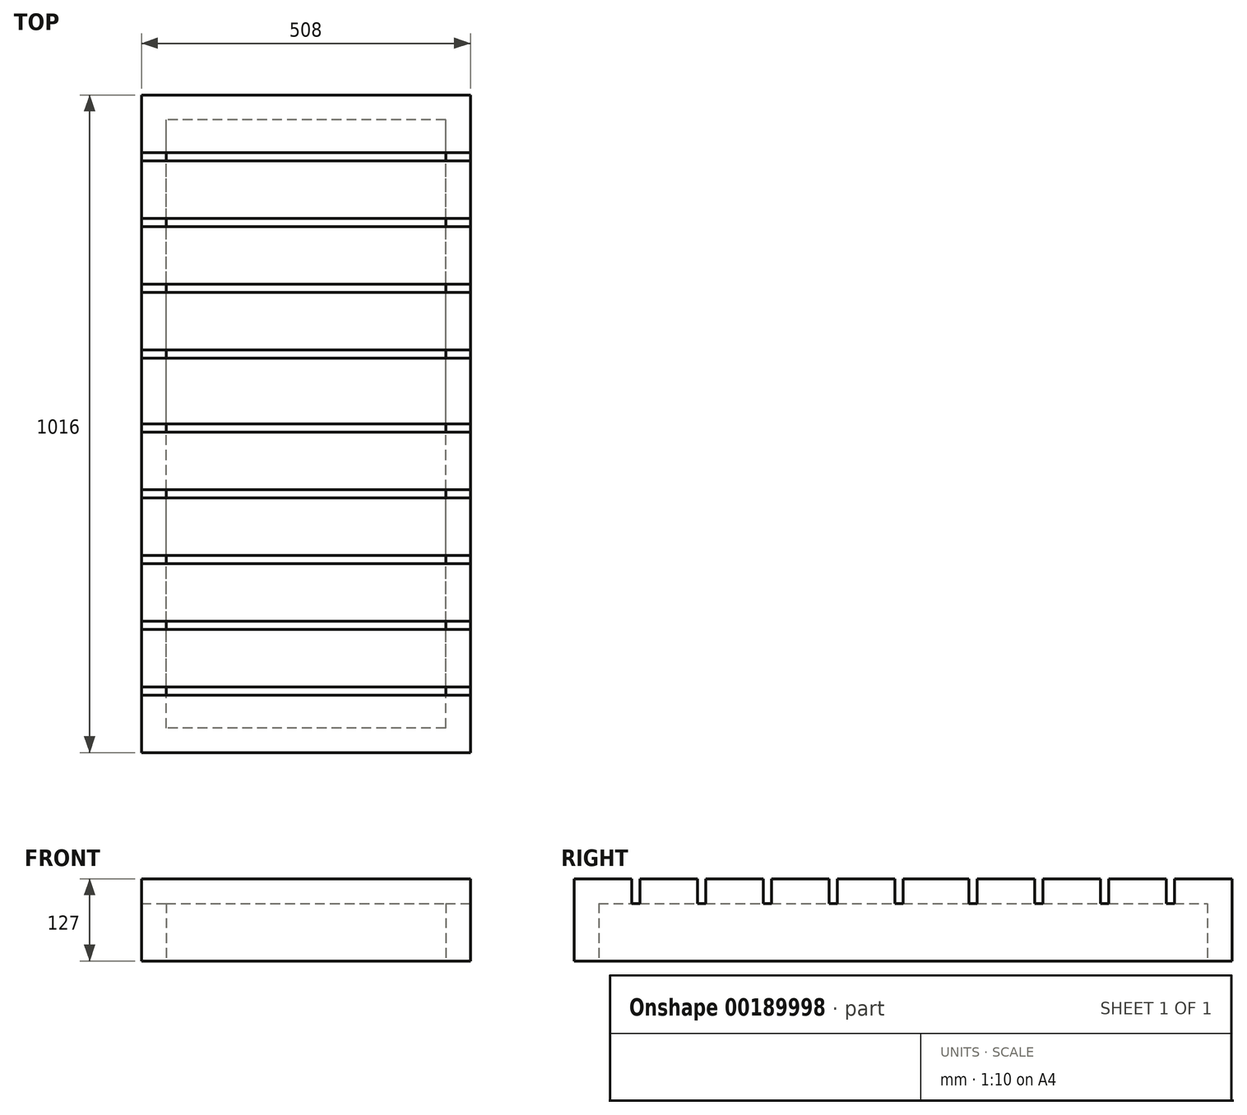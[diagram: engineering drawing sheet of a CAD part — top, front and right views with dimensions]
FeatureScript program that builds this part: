
annotation { "Feature Type Name" : "Feature", "Feature Type Description" : "" }
export const myFeature = defineFeature(function(context is Context, id is Id, definition is map)
    precondition{}
    {
        {
            var Q0;
            Q0=qCreatedBy(makeId("Top.planeOp"),FACE);
            var sketch = newSketch(context, id + "F0", { "sketchPlane" : qUnion([Q0])});
            skLineSegment(sketch, "E0.bottom", {"start": v(254, 508) * mm, "end": v(-254, 508) * mm});
            skLineSegment(sketch, "E0.top", {"start": v(254, -508) * mm, "end": v(-254, -508) * mm});
            skLineSegment(sketch, "E0.left", {"start": v(254, 508) * mm, "end": v(254, -508) * mm});
            skLineSegment(sketch, "E0.right", {"start": v(-254, 508) * mm, "end": v(-254, -508) * mm});
            skPoint(sketch, "E0.middle", {"position": v(0, 0) * mm});
            skSolve(sketch);
        }
        {
            var Q0;
            Q0=makeQuery(id+"F0.imprint","IMPRINT",FACE,{"disambiguationData":[TD([[makeQuery(id+"F0.imprint","IMPRINT",EDGE,{"derivedFrom":sQuery(id+"F0.wireOp",EDGE,"E0.bottom")}),1.0]])]});
            extrude(context, id + "F1", {"entities" : qUnion([Q0]), "depth" : 88.9 * mm});
        }
        {
            var Q0;
            Q0=makeQuery(id+"F1.opExtrude","CAP_FACE",FACE,{"disambiguationData":[OSD([sQuery(id+"F0.wireOp",EDGE,"E0.bottom"),sQuery(id+"F0.wireOp",EDGE,"E0.top"),sQuery(id+"F0.wireOp",EDGE,"E0.left"),sQuery(id+"F0.wireOp",EDGE,"E0.right")])],"isStart":true});
            var sketch = newSketch(context, id + "F2", { "sketchPlane" : qUnion([Q0])});
            skLineSegment(sketch, "E1.bottom", {"start": v(215.9, 469.9) * mm, "end": v(-215.9, 469.9) * mm});
            skLineSegment(sketch, "E1.top", {"start": v(215.9, -469.9) * mm, "end": v(-215.9, -469.9) * mm});
            skLineSegment(sketch, "E1.left", {"start": v(215.9, 469.9) * mm, "end": v(215.9, -469.9) * mm});
            skLineSegment(sketch, "E1.right", {"start": v(-215.9, 469.9) * mm, "end": v(-215.9, -469.9) * mm});
            skSolve(sketch);
        }
        {
            var Q0;
            Q0 = qSketchRegion(id + "F2", true);
            extrude(context, id + "F6", {"entities" : qUnion([Q0]), "operationType" : NewBodyOperationType.REMOVE, "oppositeDirection" : true, "depth" : 88.9 * mm});
        }
        {
            var Q0;
            Q0=makeQuery(id+"F1.opExtrude","CAP_FACE",FACE,{"disambiguationData":[OSD([sQuery(id+"F0.wireOp",EDGE,"E0.bottom"),sQuery(id+"F0.wireOp",EDGE,"E0.top"),sQuery(id+"F0.wireOp",EDGE,"E0.left"),sQuery(id+"F0.wireOp",EDGE,"E0.right")])],"isStart":false});
            var sketch = newSketch(context, id + "F3", { "sketchPlane" : qUnion([Q0])});
            skLineSegment(sketch, "E2.bottom", {"start": v(-254, 508) * mm, "end": v(254, 508) * mm});
            skLineSegment(sketch, "E2.left", {"start": v(-254, 508) * mm, "end": v(-254, -508) * mm});
            skLineSegment(sketch, "E2.right", {"start": v(254, 508) * mm, "end": v(254, -508) * mm});
            skLineSegment(sketch, "E3", {"start": v(-254, -508) * mm, "end": v(254, -508) * mm});
            skSolve(sketch);
        }
        {
            var Q0;
            Q0 = qSketchRegion(id + "F3", true);
            extrude(context, id + "F4", {"entities" : qUnion([Q0]), "operationType" : NewBodyOperationType.ADD, "depth" : 38.1 * mm});
        }
        {
            var Q0;
            Q0=makeQuery(id+"F4.opExtrude","CAP_FACE",FACE,{"disambiguationData":[OSD([sQuery(id+"F3.wireOp",EDGE,"E2.bottom"),sQuery(id+"F3.wireOp",EDGE,"E2.left"),sQuery(id+"F3.wireOp",EDGE,"E2.right"),sQuery(id+"F3.wireOp",EDGE,"E3")])],"isStart":false});
            var sketch = newSketch(context, id + "F5", { "sketchPlane" : qUnion([Q0])});
            skLineSegment(sketch, "E4.bottom", {"start": v(-254, 419.1) * mm, "end": v(254, 419.1) * mm});
            skLineSegment(sketch, "E4.top", {"start": v(-254, 406.4) * mm, "end": v(254, 406.4) * mm});
            skLineSegment(sketch, "E4.left", {"start": v(-254, 419.1) * mm, "end": v(-254, 406.4) * mm});
            skLineSegment(sketch, "E4.right", {"start": v(254, 419.1) * mm, "end": v(254, 406.4) * mm});
            skLineSegment(sketch, "E5.bottom", {"start": v(-254, 317.5) * mm, "end": v(254, 317.5) * mm});
            skLineSegment(sketch, "E5.top", {"start": v(-254, 304.8) * mm, "end": v(254, 304.8) * mm});
            skLineSegment(sketch, "E5.left", {"start": v(-254, 317.5) * mm, "end": v(-254, 304.8) * mm});
            skLineSegment(sketch, "E5.right", {"start": v(254, 317.5) * mm, "end": v(254, 304.8) * mm});
            skLineSegment(sketch, "E6.bottom", {"start": v(-254, 215.9) * mm, "end": v(254, 215.9) * mm});
            skLineSegment(sketch, "E6.top", {"start": v(-254, 203.2) * mm, "end": v(254, 203.2) * mm});
            skLineSegment(sketch, "E6.left", {"start": v(-254, 215.9) * mm, "end": v(-254, 203.2) * mm});
            skLineSegment(sketch, "E6.right", {"start": v(254, 215.9) * mm, "end": v(254, 203.2) * mm});
            skLineSegment(sketch, "E7.bottom", {"start": v(-254, 114.3) * mm, "end": v(254, 114.3) * mm});
            skLineSegment(sketch, "E7.top", {"start": v(-254, 101.6) * mm, "end": v(254, 101.6) * mm});
            skLineSegment(sketch, "E7.left", {"start": v(-254, 114.3) * mm, "end": v(-254, 101.6) * mm});
            skLineSegment(sketch, "E7.right", {"start": v(254, 114.3) * mm, "end": v(254, 101.6) * mm});
            skLineSegment(sketch, "E8.bottom", {"start": v(-254, 0) * mm, "end": v(254, 0) * mm});
            skLineSegment(sketch, "E8.top", {"start": v(-254, -12.7) * mm, "end": v(254, -12.7) * mm});
            skLineSegment(sketch, "E8.left", {"start": v(-254, 0) * mm, "end": v(-254, -12.7) * mm});
            skLineSegment(sketch, "E8.right", {"start": v(254, 0) * mm, "end": v(254, -12.7) * mm});
            skLineSegment(sketch, "E9.bottom", {"start": v(-254, -101.6) * mm, "end": v(254, -101.6) * mm});
            skLineSegment(sketch, "E9.top", {"start": v(-254, -114.3) * mm, "end": v(254, -114.3) * mm});
            skLineSegment(sketch, "E9.left", {"start": v(-254, -101.6) * mm, "end": v(-254, -114.3) * mm});
            skLineSegment(sketch, "E9.right", {"start": v(254, -101.6) * mm, "end": v(254, -114.3) * mm});
            skLineSegment(sketch, "E10.bottom", {"start": v(-254, -203.2) * mm, "end": v(254, -203.2) * mm});
            skLineSegment(sketch, "E10.top", {"start": v(-254, -215.9) * mm, "end": v(254, -215.9) * mm});
            skLineSegment(sketch, "E10.left", {"start": v(-254, -203.2) * mm, "end": v(-254, -215.9) * mm});
            skLineSegment(sketch, "E10.right", {"start": v(254, -203.2) * mm, "end": v(254, -215.9) * mm});
            skLineSegment(sketch, "E11.bottom", {"start": v(-254, -304.8) * mm, "end": v(254, -304.8) * mm});
            skLineSegment(sketch, "E11.top", {"start": v(-254, -317.5) * mm, "end": v(254, -317.5) * mm});
            skLineSegment(sketch, "E11.left", {"start": v(-254, -304.8) * mm, "end": v(-254, -317.5) * mm});
            skLineSegment(sketch, "E11.right", {"start": v(254, -304.8) * mm, "end": v(254, -317.5) * mm});
            skLineSegment(sketch, "E12.bottom", {"start": v(-254, -406.4) * mm, "end": v(254, -406.4) * mm});
            skLineSegment(sketch, "E12.top", {"start": v(-254, -419.1) * mm, "end": v(254, -419.1) * mm});
            skLineSegment(sketch, "E12.left", {"start": v(-254, -406.4) * mm, "end": v(-254, -419.1) * mm});
            skLineSegment(sketch, "E12.right", {"start": v(254, -406.4) * mm, "end": v(254, -419.1) * mm});
            skSolve(sketch);
        }
        {
            var Q0;
            Q0 = qSketchRegion(id + "F5", true);
            extrude(context, id + "F7", {"entities" : qUnion([Q0]), "operationType" : NewBodyOperationType.REMOVE, "oppositeDirection" : true, "depth" : 38.1 * mm});
        }
    });
